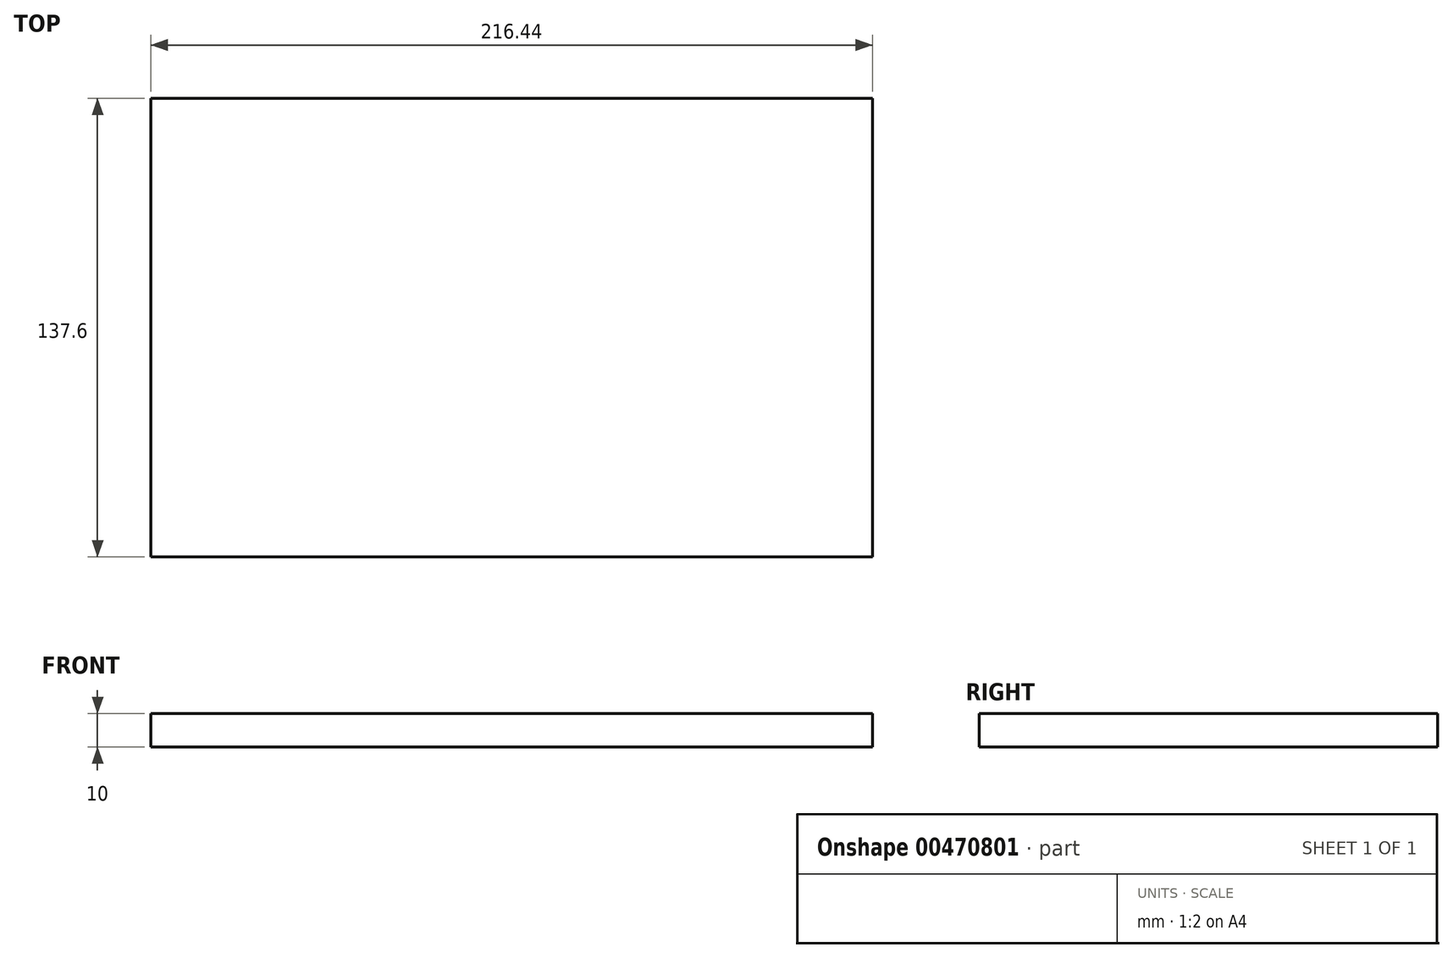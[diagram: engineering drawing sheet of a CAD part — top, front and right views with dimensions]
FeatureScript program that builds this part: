
annotation { "Feature Type Name" : "Feature", "Feature Type Description" : "" }
export const myFeature = defineFeature(function(context is Context, id is Id, definition is map)
    precondition{}
    {
        {
            var Q0;
            Q0=qCreatedBy(makeId("Top.planeOp"),FACE);
            var sketch = newSketch(context, id + "F0", { "sketchPlane" : qUnion([Q0])});
            skLineSegment(sketch, "E0.bottom", {"start": v(-108.22, 68.8) * mm, "end": v(108.22, 68.8) * mm});
            skLineSegment(sketch, "E0.top", {"start": v(-108.22, -68.8) * mm, "end": v(108.22, -68.8) * mm});
            skLineSegment(sketch, "E0.left", {"start": v(-108.22, 68.8) * mm, "end": v(-108.22, -68.8) * mm});
            skLineSegment(sketch, "E0.right", {"start": v(108.22, 68.8) * mm, "end": v(108.22, -68.8) * mm});
            skPoint(sketch, "E0.middle", {"position": v(0, 0) * mm});
            skSolve(sketch);
        }
        {
            var Q0;
            Q0 = qSketchRegion(id + "F0", true);
            extrude(context, id + "F1", {"entities" : qUnion([Q0]), "endBound" : BoundingType.SYMMETRIC, "depth" : 10 * mm});
        }
    });
